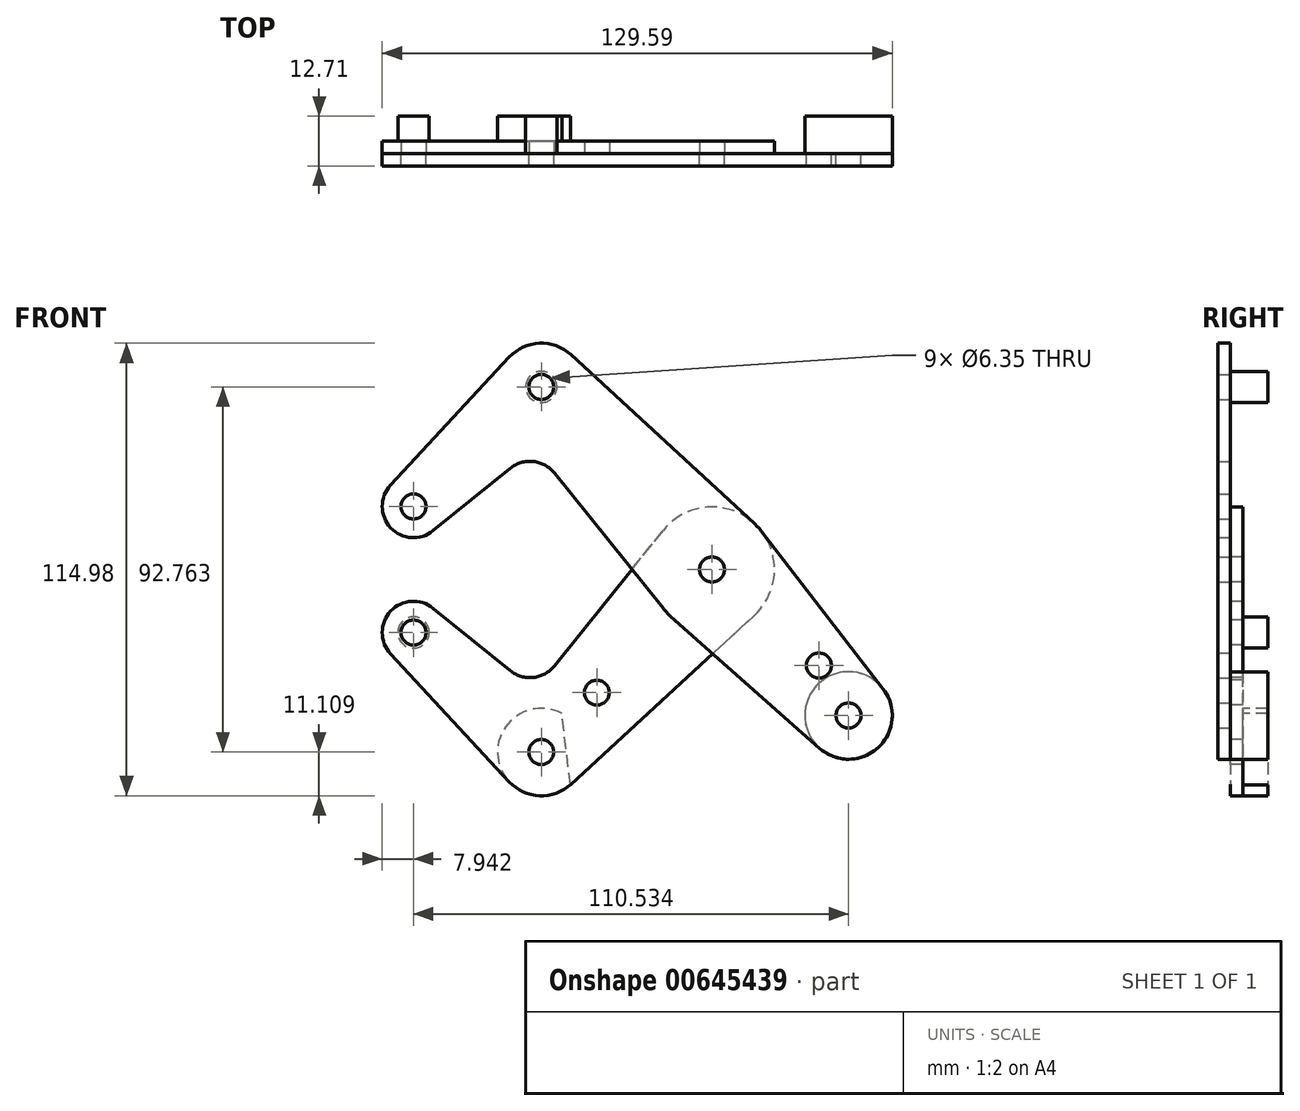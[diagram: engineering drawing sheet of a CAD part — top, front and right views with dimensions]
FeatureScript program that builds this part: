
annotation { "Feature Type Name" : "Feature", "Feature Type Description" : "" }
export const myFeature = defineFeature(function(context is Context, id is Id, definition is map)
    precondition{}
    {
        {
            var Q0;
            Q0=qCreatedBy(makeId("Front.planeOp"),FACE);
            var sketch = newSketch(context, id + "F0", { "sketchPlane" : qUnion([Q0])});
            skLineSegment(sketch, "E0", {"start": v(-75.84, 16.02) * mm, "end": v(-43.37, 46.38) * mm, "construction": true});
            skLineSegment(sketch, "E1", {"start": v(-43.37, 46.38) * mm, "end": v(34.7, -37.1) * mm, "construction": true});
            skCircle(sketch, "E2", {"center": v(-75.84, 16.02) * mm, "radius": 7.94 * mm});
            skCircle(sketch, "E3", {"center": v(-75.84, 16.02) * mm, "radius": 3.18 * mm});
            skCircle(sketch, "E4", {"center": v(-43.37, 46.38) * mm, "radius": 11.11 * mm});
            skCircle(sketch, "E5", {"center": v(-43.37, 46.38) * mm, "radius": 3.18 * mm});
            skCircle(sketch, "E6", {"center": v(0, 0) * mm, "radius": 15.88 * mm});
            skCircle(sketch, "E7", {"center": v(0, 0) * mm, "radius": 3.98 * mm});
            skCircle(sketch, "E8", {"center": v(0, 0) * mm, "radius": 3.18 * mm});
            skCircle(sketch, "E9", {"center": v(34.7, -37.1) * mm, "radius": 11.11 * mm});
            skCircle(sketch, "E10", {"center": v(34.7, -37.1) * mm, "radius": 3.18 * mm});
            skCircle(sketch, "E11", {"center": v(27.17, -24.4) * mm, "radius": 3.18 * mm});
            skLineSegment(sketch, "E12", {"start": v(-81.66, 21.42) * mm, "end": v(-51.52, 53.94) * mm});
            skLineSegment(sketch, "E13", {"start": v(-70.84, 9.85) * mm, "end": v(-51.25, 25.7) * mm});
            skLineSegment(sketch, "E14", {"start": v(-35.85, 54.56) * mm, "end": v(10.75, 11.68) * mm});
            skLineSegment(sketch, "E15", {"start": v(12.56, 9.7) * mm, "end": v(43.49, -30.3) * mm});
            skLineSegment(sketch, "E16", {"start": v(-40.05, 24.5) * mm, "end": v(-12.38, -9.94) * mm});
            skLineSegment(sketch, "E17", {"start": v(-10.53, -11.88) * mm, "end": v(27.33, -45.42) * mm});
            skArc(sketch, "E18.filletArc", {"start": v(-40.05, 24.5) * mm, "mid": v(-45.4, 27.43) * mm, "end": v(-51.25, 25.7) * mm});
            skLineSegment(sketch, "E19", {"start": v(0, 0) * mm, "end": v(-43.37, -46.38) * mm, "construction": true});
            skLineSegment(sketch, "E20", {"start": v(-43.37, -46.38) * mm, "end": v(-75.84, -16.02) * mm, "construction": true});
            skCircle(sketch, "E21", {"center": v(-75.84, -16.02) * mm, "radius": 7.94 * mm});
            skCircle(sketch, "E22", {"center": v(-75.84, -16.02) * mm, "radius": 3.18 * mm});
            skCircle(sketch, "E23", {"center": v(-43.37, -46.38) * mm, "radius": 11.11 * mm});
            skCircle(sketch, "E24", {"center": v(-43.37, -46.38) * mm, "radius": 3.18 * mm});
            skCircle(sketch, "E25", {"center": v(-29.27, -31.3) * mm, "radius": 3.18 * mm});
            skLineSegment(sketch, "E26", {"start": v(-81.66, -21.42) * mm, "end": v(-51.52, -53.94) * mm});
            skLineSegment(sketch, "E27", {"start": v(-70.84, -9.85) * mm, "end": v(-51.25, -25.7) * mm});
            skLineSegment(sketch, "E28", {"start": v(-35.85, -54.56) * mm, "end": v(10.75, -11.68) * mm});
            skLineSegment(sketch, "E29", {"start": v(-40.05, -24.5) * mm, "end": v(-12.38, 9.94) * mm});
            skArc(sketch, "E30.filletArc", {"start": v(-51.25, -25.7) * mm, "mid": v(-45.4, -27.43) * mm, "end": v(-40.05, -24.5) * mm});
            skSolve(sketch);
        }
        {
            var Q0;
            Q0=makeQuery(id+"F0.imprint","IMPRINT",FACE,{"disambiguationData":[TD([[makeQuery(id+"F0.imprint","IMPRINT",EDGE,{"derivedFrom":sQuery(id+"F0.wireOp",EDGE,"E3")}),-1.0]])]});
            var Q1;
            {var subQ0=sQuery(id+"F0.wireOp",EDGE,"E12");Q1=makeQuery(id+"F0.imprint","IMPRINT",FACE,{"disambiguationData":[TD([[makeQuery(id+"F0.imprint","IMPRINT",EDGE,{"derivedFrom":subQ0}),-1.0]])]});}
            var Q2;
            {var subQ0=sQuery(id+"F0.wireOp",EDGE,"E16");var subQ1=sQuery(id+"F0.wireOp",EDGE,"E6");var subQ2=makeQuery(id+"F0.imprint","INTERSECT",VERTEX,{"derivedFrom":[subQ1,subQ0]});Q2=makeQuery(id+"F0.imprint","IMPRINT",FACE,{"disambiguationData":[TD([[makeQuery(id+"F0.imprint","IMPRINT",EDGE,{"disambiguationData":[TD([[subQ2,1.0]])],"derivedFrom":subQ1}),-1.0]])]});}
            var Q3;
            Q3=makeQuery(id+"F0.imprint","IMPRINT",FACE,{"disambiguationData":[TD([[makeQuery(id+"F0.imprint","IMPRINT",EDGE,{"derivedFrom":sQuery(id+"F0.wireOp",EDGE,"E11")}),-1.0]])]});
            var Q4;
            {var subQ0=sQuery(id+"F0.wireOp",EDGE,"E17");var subQ1=sQuery(id+"F0.wireOp",EDGE,"E6");var subQ2=makeQuery(id+"F0.imprint","INTERSECT",VERTEX,{"derivedFrom":[subQ1,subQ0]});Q4=makeQuery(id+"F0.imprint","IMPRINT",FACE,{"disambiguationData":[TD([[makeQuery(id+"F0.imprint","IMPRINT",EDGE,{"disambiguationData":[TD([[subQ2,-1.0]])],"derivedFrom":subQ1}),-1.0]])]});}
            var Q5;
            Q5=makeQuery(id+"F0.imprint","IMPRINT",FACE,{"disambiguationData":[TD([[makeQuery(id+"F0.imprint","IMPRINT",EDGE,{"derivedFrom":sQuery(id+"F0.wireOp",EDGE,"E7")}),-1.0]])]});
            var Q6;
            Q6=makeQuery(id+"F0.imprint","IMPRINT",FACE,{"disambiguationData":[TD([[makeQuery(id+"F0.imprint","IMPRINT",EDGE,{"derivedFrom":sQuery(id+"F0.wireOp",EDGE,"E7")}),1.0]])]});
            var Q7;
            Q7=makeQuery(id+"F0.imprint","IMPRINT",FACE,{"disambiguationData":[TD([[makeQuery(id+"F0.imprint","IMPRINT",EDGE,{"derivedFrom":sQuery(id+"F0.wireOp",EDGE,"E10")}),-1.0]])]});
            var Q8;
            Q8=makeQuery(id+"F0.imprint","IMPRINT",FACE,{"disambiguationData":[TD([[makeQuery(id+"F0.imprint","IMPRINT",EDGE,{"derivedFrom":sQuery(id+"F0.wireOp",EDGE,"E5")}),-1.0]])]});
            extrude(context, id + "F1", {"entities" : qUnion([Q0, Q1, Q2, Q3, Q4, Q5, Q6, Q7, Q8]), "depth" : 3.17 * mm, "offsetDistance" : 25.4 * mm});
        }
        {
            var Q0;
            Q0=makeQuery(id+"F0.imprint","IMPRINT",FACE,{"disambiguationData":[TD([[makeQuery(id+"F0.imprint","IMPRINT",EDGE,{"derivedFrom":sQuery(id+"F0.wireOp",EDGE,"E22")}),-1.0]])]});
            var Q1;
            Q1=makeQuery(id+"F0.imprint","IMPRINT",FACE,{"disambiguationData":[TD([[makeQuery(id+"F0.imprint","IMPRINT",EDGE,{"derivedFrom":sQuery(id+"F0.wireOp",EDGE,"E25")}),-1.0]])]});
            var Q2;
            {var subQ0=sQuery(id+"F0.wireOp",EDGE,"E17");var subQ1=sQuery(id+"F0.wireOp",EDGE,"E6");var subQ2=makeQuery(id+"F0.imprint","INTERSECT",VERTEX,{"derivedFrom":[subQ1,subQ0]});Q2=makeQuery(id+"F0.imprint","IMPRINT",FACE,{"disambiguationData":[TD([[makeQuery(id+"F0.imprint","IMPRINT",EDGE,{"disambiguationData":[TD([[subQ2,-1.0]])],"derivedFrom":subQ1}),-1.0]])]});}
            var Q3;
            {var subQ0=sQuery(id+"F0.wireOp",EDGE,"E16");var subQ1=sQuery(id+"F0.wireOp",EDGE,"E6");var subQ2=makeQuery(id+"F0.imprint","INTERSECT",VERTEX,{"derivedFrom":[subQ1,subQ0]});Q3=makeQuery(id+"F0.imprint","IMPRINT",FACE,{"disambiguationData":[TD([[makeQuery(id+"F0.imprint","IMPRINT",EDGE,{"disambiguationData":[TD([[subQ2,1.0]])],"derivedFrom":subQ1}),-1.0]])]});}
            var Q4;
            Q4=makeQuery(id+"F0.imprint","IMPRINT",FACE,{"disambiguationData":[TD([[makeQuery(id+"F0.imprint","IMPRINT",EDGE,{"derivedFrom":sQuery(id+"F0.wireOp",EDGE,"E7")}),-1.0]])]});
            var Q5;
            Q5=makeQuery(id+"F0.imprint","IMPRINT",FACE,{"disambiguationData":[TD([[makeQuery(id+"F0.imprint","IMPRINT",EDGE,{"derivedFrom":sQuery(id+"F0.wireOp",EDGE,"E7")}),1.0]])]});
            var Q6;
            Q6=makeQuery(id+"F0.imprint","IMPRINT",FACE,{"disambiguationData":[TD([[makeQuery(id+"F0.imprint","IMPRINT",EDGE,{"derivedFrom":sQuery(id+"F0.wireOp",EDGE,"E24")}),-1.0]])]});
            extrude(context, id + "F2", {"entities" : qUnion([Q0, Q1, Q2, Q3, Q4, Q5, Q6]), "oppositeDirection" : true, "depth" : 3.17 * mm, "offsetDistance" : 25.4 * mm});
        }
        {
            var Q0;
            Q0=makeQuery(id+"F1.opExtrude","CAP_FACE",FACE,{"disambiguationData":[OSD([sQuery(id+"F0.wireOp",EDGE,"E2"),sQuery(id+"F0.wireOp",EDGE,"E3"),sQuery(id+"F0.wireOp",EDGE,"E4"),sQuery(id+"F0.wireOp",EDGE,"E5"),sQuery(id+"F0.wireOp",EDGE,"E6"),sQuery(id+"F0.wireOp",EDGE,"E8"),sQuery(id+"F0.wireOp",EDGE,"E9"),sQuery(id+"F0.wireOp",EDGE,"E10"),sQuery(id+"F0.wireOp",EDGE,"E11"),sQuery(id+"F0.wireOp",EDGE,"E12"),sQuery(id+"F0.wireOp",EDGE,"E13"),sQuery(id+"F0.wireOp",EDGE,"E14"),sQuery(id+"F0.wireOp",EDGE,"E15"),sQuery(id+"F0.wireOp",EDGE,"E16"),sQuery(id+"F0.wireOp",EDGE,"E17"),sQuery(id+"F0.wireOp",EDGE,"E18.filletArc")])],"isStart":false});
            var sketch = newSketch(context, id + "F3", { "sketchPlane" : qUnion([Q0])});
            skCircle(sketch, "E31", {"center": v(-43.37, 46.38) * mm, "radius": 3.98 * mm});
            skCircle(sketch, "E32.0", {"center": v(34.7, -37.1) * mm, "radius": 11.11 * mm});
            skSolve(sketch);
        }
        {
            var Q0;
            Q0=makeQuery(id+"F0.imprint","IMPRINT",FACE,{"disambiguationData":[TD([[makeQuery(id+"F0.imprint","IMPRINT",EDGE,{"derivedFrom":sQuery(id+"F0.wireOp",EDGE,"E22")}),-1.0]])]});
            var sketch = newSketch(context, id + "F4", { "sketchPlane" : qUnion([Q0])});
            skCircle(sketch, "E33", {"center": v(-75.84, -16.02) * mm, "radius": 3.98 * mm});
            skArc(sketch, "E34.0", {"start": v(-38.14, -36.58) * mm, "mid": v(-54.4, -47.7) * mm, "end": v(-35.99, -54.69) * mm});
            skLineSegment(sketch, "E35", {"start": v(-43.37, -46.38) * mm, "end": v(34.7, -37.1) * mm, "construction": true});
            skLineSegment(sketch, "E36", {"start": v(-38.14, -36.58) * mm, "end": v(-35.99, -54.69) * mm});
            skSolve(sketch);
        }
        {
            var Q0;
            Q0=qCreatedBy(makeId("Front.planeOp"),FACE);
            cPlane(context, id + "F5", {"entities" : qUnion([Q0]), "cplaneType" : CPlaneType.OFFSET, "offset" : 9.52 * mm, "oppositeDirection" : true, "width" : 152.4 * mm, "height" : 152.4 * mm});
        }
        {
            var Q0;
            Q0 = qSketchRegion(id + "F3", true);
            var Q1;
            Q1 = qSketchRegion(id + "F4", true);
            var Q2;
            Q2=qCreatedBy(id+"F5.planeOp",FACE);
            extrude(context, id + "F6", {"entities" : qUnion([Q0, Q1]), "endBound" : BoundingType.UP_TO_SURFACE, "oppositeDirection" : true, "depth" : 25.4 * mm, "endBoundEntityFace" : qUnion([Q2]), "offsetDistance" : 25.4 * mm});
        }
        {
            var Q0;
            Q0=makeQuery(id+"F1.opExtrude","SWEPT_BODY",BODY,{"disambiguationData":[OSD([sQuery(id+"F0.wireOp",EDGE,"E2"),sQuery(id+"F0.wireOp",EDGE,"E3"),sQuery(id+"F0.wireOp",EDGE,"E4"),sQuery(id+"F0.wireOp",EDGE,"E5"),sQuery(id+"F0.wireOp",EDGE,"E6"),sQuery(id+"F0.wireOp",EDGE,"E8"),sQuery(id+"F0.wireOp",EDGE,"E9"),sQuery(id+"F0.wireOp",EDGE,"E10"),sQuery(id+"F0.wireOp",EDGE,"E11"),sQuery(id+"F0.wireOp",EDGE,"E12"),sQuery(id+"F0.wireOp",EDGE,"E13"),sQuery(id+"F0.wireOp",EDGE,"E14"),sQuery(id+"F0.wireOp",EDGE,"E15"),sQuery(id+"F0.wireOp",EDGE,"E16"),sQuery(id+"F0.wireOp",EDGE,"E17"),sQuery(id+"F0.wireOp",EDGE,"E18.filletArc")])]});
            var Q1;
            Q1=makeQuery(id+"F2.opExtrude","SWEPT_BODY",BODY,{"disambiguationData":[OSD([sQuery(id+"F0.wireOp",EDGE,"E6"),sQuery(id+"F0.wireOp",EDGE,"E8"),sQuery(id+"F0.wireOp",EDGE,"E21"),sQuery(id+"F0.wireOp",EDGE,"E22"),sQuery(id+"F0.wireOp",EDGE,"E23"),sQuery(id+"F0.wireOp",EDGE,"E24"),sQuery(id+"F0.wireOp",EDGE,"E25"),sQuery(id+"F0.wireOp",EDGE,"E26"),sQuery(id+"F0.wireOp",EDGE,"E27"),sQuery(id+"F0.wireOp",EDGE,"E28"),sQuery(id+"F0.wireOp",EDGE,"E29"),sQuery(id+"F0.wireOp",EDGE,"E30.filletArc")])]});
            var Q2;
            Q2=makeQuery(id+"F6.opExtrude","SWEPT_BODY",BODY,{"disambiguationData":[OSD([sQuery(id+"F3.wireOp",EDGE,"E32.0")])]});
            var Q3;
            Q3=makeQuery(id+"F6.opExtrude","SWEPT_BODY",BODY,{"disambiguationData":[OSD([sQuery(id+"F3.wireOp",EDGE,"E31")])]});
            var Q4;
            Q4=makeQuery(id+"F6.opExtrude","SWEPT_BODY",BODY,{"disambiguationData":[OSD([sQuery(id+"F4.wireOp",EDGE,"E33")])]});
            var Q5;
            Q5=makeQuery(id+"F6.opExtrude","SWEPT_BODY",BODY,{"disambiguationData":[OSD([sQuery(id+"F4.wireOp",EDGE,"E34.0"),sQuery(id+"F4.wireOp",EDGE,"E36")])]});
            booleanBodies(context, id + "F7", {"operationType" : BooleanOperationType.SUBTRACTION, "tools" : qUnion([Q0, Q1]), "targets" : qUnion([Q2, Q3, Q4, Q5]), "keepTools" : true});
        }
    });
